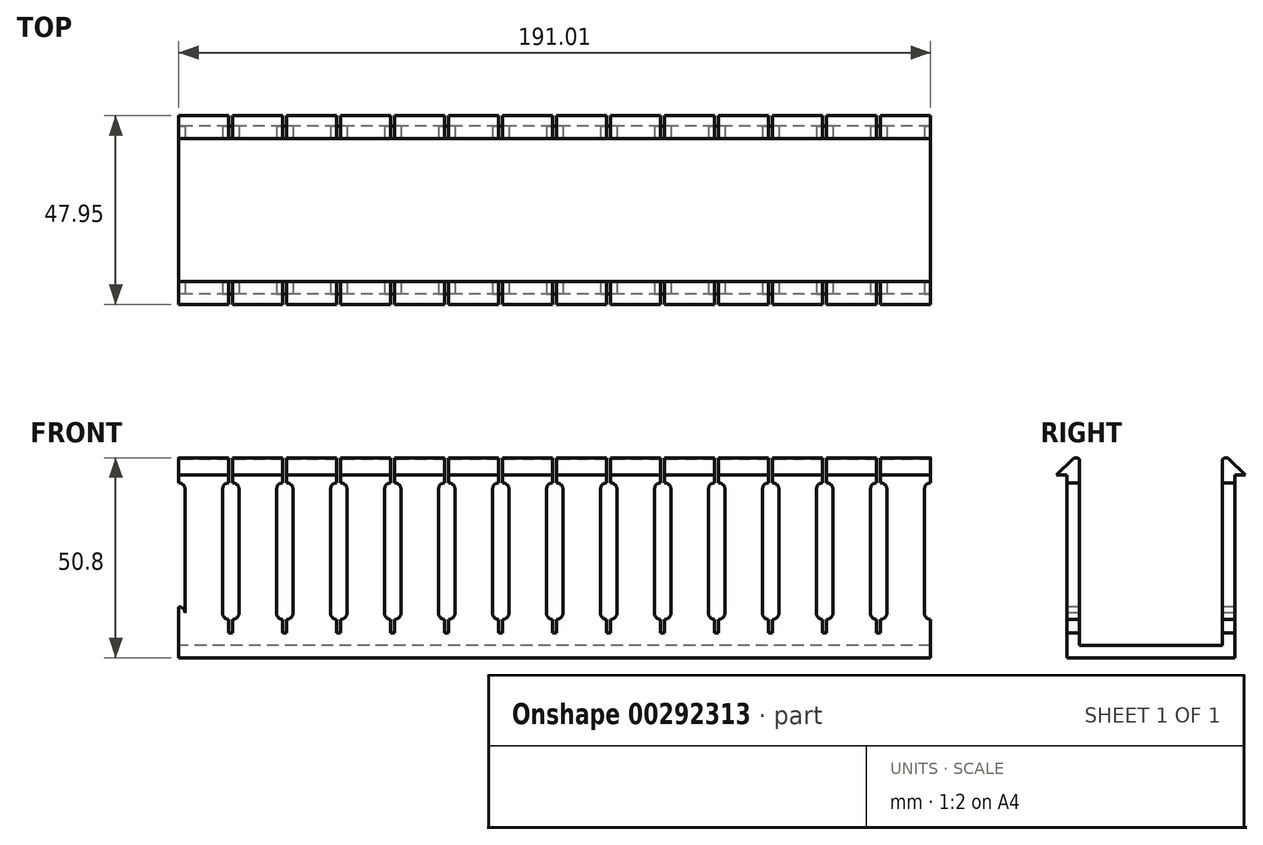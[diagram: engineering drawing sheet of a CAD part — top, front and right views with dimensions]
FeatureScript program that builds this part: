
annotation { "Feature Type Name" : "Feature", "Feature Type Description" : "" }
export const myFeature = defineFeature(function(context is Context, id is Id, definition is map)
    precondition{}
    {
        {
            var Q0;
            Q0=qCreatedBy(makeId("Right.planeOp"),FACE);
            var sketch = newSketch(context, id + "F0", { "sketchPlane" : qUnion([Q0])});
            skLineSegment(sketch, "E0", {"start": v(0, -0.02) * mm, "end": v(0, 46.4) * mm});
            skLineSegment(sketch, "E1", {"start": v(0, 46.4) * mm, "end": v(-2.64, 46.4) * mm});
            skLineSegment(sketch, "E2", {"start": v(-2.64, 46.4) * mm, "end": v(1.38, 50.43) * mm});
            skArc(sketch, "E3", {"start": v(3.17, 50.43) * mm, "mid": v(2.28, 50.8) * mm, "end": v(1.38, 50.43) * mm});
            skLineSegment(sketch, "E4", {"start": v(3.17, 50.43) * mm, "end": v(3.18, 3.18) * mm});
            skLineSegment(sketch, "E5", {"start": v(3.18, 3.18) * mm, "end": v(39.5, 3.18) * mm});
            skLineSegment(sketch, "E6", {"start": v(39.5, 3.18) * mm, "end": v(39.5, 50.43) * mm});
            skArc(sketch, "E7", {"start": v(41.3, 50.43) * mm, "mid": v(40.4, 50.8) * mm, "end": v(39.5, 50.43) * mm});
            skLineSegment(sketch, "E8", {"start": v(41.3, 50.43) * mm, "end": v(45.31, 46.4) * mm});
            skLineSegment(sketch, "E9", {"start": v(45.31, 46.4) * mm, "end": v(42.67, 46.4) * mm});
            skLineSegment(sketch, "E10", {"start": v(42.67, 46.4) * mm, "end": v(42.67, 0) * mm});
            skLineSegment(sketch, "E11", {"start": v(42.67, 0) * mm, "end": v(0, 0) * mm});
            skSolve(sketch);
        }
        {
            var Q0;
            {var subQ0=sQuery(id+"F0.wireOp",EDGE,"E1");Q0=makeQuery(id+"F0.imprint","IMPRINT",FACE,{"disambiguationData":[TD([[makeQuery(id+"F0.imprint","IMPRINT",EDGE,{"derivedFrom":subQ0}),-1.0]])]});}
            extrude(context, id + "F1", {"entities" : qUnion([Q0]), "depth" : 191 * mm});
        }
        {
            var Q0;
            Q0=makeQuery(id+"F1.opExtrude","SWEPT_FACE",FACE,{"disambiguationData":[OSD([sQuery(id+"F0.wireOp",EDGE,"E0")])]});
            var sketch = newSketch(context, id + "F2", { "sketchPlane" : qUnion([Q0])});
            skLineSegment(sketch, "E12", {"start": v(1.59, 42.86) * mm, "end": v(1.59, 11.37) * mm});
            skLineSegment(sketch, "E13", {"start": v(12.7, 50.8) * mm, "end": v(13.72, 50.8) * mm});
            skPoint(sketch, "E14", {"position": v(0, 44.45) * mm});
            skLineSegment(sketch, "E15", {"start": v(0, 44.45) * mm, "end": v(12.7, 44.45) * mm});
            skLineSegment(sketch, "E16", {"start": v(12.7, 50.8) * mm, "end": v(12.7, 44.45) * mm});
            skLineSegment(sketch, "E17", {"start": v(13.72, 50.8) * mm, "end": v(13.72, 44.45) * mm});
            skLineSegment(sketch, "E18", {"start": v(11.11, 42.86) * mm, "end": v(11.11, 11.37) * mm});
            skLineSegment(sketch, "E19", {"start": v(0, 42.86) * mm, "end": v(0, 12.94) * mm});
            skArc(sketch, "E20", {"start": v(1.59, 11.37) * mm, "mid": v(1.12, 12.48) * mm, "end": v(0, 12.94) * mm});
            skArc(sketch, "E21", {"start": v(12.7, 44.45) * mm, "mid": v(11.58, 43.99) * mm, "end": v(11.11, 42.86) * mm});
            skArc(sketch, "E22", {"start": v(15.3, 42.86) * mm, "mid": v(14.84, 43.99) * mm, "end": v(13.72, 44.45) * mm});
            skLineSegment(sketch, "E23", {"start": v(15.3, 42.86) * mm, "end": v(15.3, 11.37) * mm});
            skArc(sketch, "E24", {"start": v(13.72, 9.78) * mm, "mid": v(14.84, 10.24) * mm, "end": v(15.3, 11.37) * mm});
            skLineSegment(sketch, "E25", {"start": v(12.67, 6.3) * mm, "end": v(13.72, 6.3) * mm});
            skLineSegment(sketch, "E26", {"start": v(13.72, 6.3) * mm, "end": v(13.72, 9.78) * mm});
            skLineSegment(sketch, "E27", {"start": v(12.67, 6.3) * mm, "end": v(12.67, 9.78) * mm});
            skArc(sketch, "E28.trimOffspring", {"start": v(11.11, 11.37) * mm, "mid": v(11.57, 10.26) * mm, "end": v(12.67, 9.78) * mm});
            skArc(sketch, "E29.1.0.0", {"start": v(24.83, 11.37) * mm, "mid": v(25.28, 10.26) * mm, "end": v(26.38, 9.78) * mm});
            skLineSegment(sketch, "E29.1.0.1", {"start": v(29.02, 42.86) * mm, "end": v(29.02, 11.37) * mm});
            skArc(sketch, "E29.1.0.2", {"start": v(26.42, 44.45) * mm, "mid": v(25.3, 43.99) * mm, "end": v(24.83, 42.86) * mm});
            skArc(sketch, "E29.1.0.3", {"start": v(29.02, 42.86) * mm, "mid": v(28.55, 43.99) * mm, "end": v(27.43, 44.45) * mm});
            skLineSegment(sketch, "E29.1.0.4", {"start": v(27.43, 50.8) * mm, "end": v(27.43, 44.45) * mm});
            skLineSegment(sketch, "E29.1.0.5", {"start": v(24.83, 42.86) * mm, "end": v(24.83, 11.37) * mm});
            skLineSegment(sketch, "E29.1.0.6", {"start": v(26.38, 6.3) * mm, "end": v(26.38, 9.78) * mm});
            skLineSegment(sketch, "E29.1.0.7", {"start": v(26.42, 50.8) * mm, "end": v(26.42, 44.45) * mm});
            skLineSegment(sketch, "E29.1.0.8", {"start": v(27.43, 6.3) * mm, "end": v(27.43, 9.78) * mm});
            skLineSegment(sketch, "E29.1.0.9", {"start": v(26.42, 50.8) * mm, "end": v(27.43, 50.8) * mm});
            skLineSegment(sketch, "E29.1.0.10", {"start": v(26.38, 6.3) * mm, "end": v(27.43, 6.3) * mm});
            skArc(sketch, "E29.1.0.11", {"start": v(27.43, 9.78) * mm, "mid": v(28.55, 10.24) * mm, "end": v(29.02, 11.37) * mm});
            skArc(sketch, "E29.2.0.0", {"start": v(38.54, 11.37) * mm, "mid": v(39, 10.26) * mm, "end": v(40.1, 9.78) * mm});
            skLineSegment(sketch, "E29.2.0.1", {"start": v(42.74, 42.86) * mm, "end": v(42.74, 11.37) * mm});
            skArc(sketch, "E29.2.0.2", {"start": v(40.13, 44.45) * mm, "mid": v(39, 43.99) * mm, "end": v(38.54, 42.86) * mm});
            skArc(sketch, "E29.2.0.3", {"start": v(42.74, 42.86) * mm, "mid": v(42.27, 43.99) * mm, "end": v(41.15, 44.45) * mm});
            skLineSegment(sketch, "E29.2.0.4", {"start": v(41.15, 50.8) * mm, "end": v(41.15, 44.45) * mm});
            skLineSegment(sketch, "E29.2.0.5", {"start": v(38.54, 42.86) * mm, "end": v(38.54, 11.37) * mm});
            skLineSegment(sketch, "E29.2.0.6", {"start": v(40.1, 6.3) * mm, "end": v(40.1, 9.78) * mm});
            skLineSegment(sketch, "E29.2.0.7", {"start": v(40.13, 50.8) * mm, "end": v(40.13, 44.45) * mm});
            skLineSegment(sketch, "E29.2.0.8", {"start": v(41.15, 6.3) * mm, "end": v(41.15, 9.78) * mm});
            skLineSegment(sketch, "E29.2.0.9", {"start": v(40.13, 50.8) * mm, "end": v(41.15, 50.8) * mm});
            skLineSegment(sketch, "E29.2.0.10", {"start": v(40.1, 6.3) * mm, "end": v(41.15, 6.3) * mm});
            skArc(sketch, "E29.2.0.11", {"start": v(41.15, 9.78) * mm, "mid": v(42.27, 10.24) * mm, "end": v(42.74, 11.37) * mm});
            skArc(sketch, "E29.3.0.0", {"start": v(52.26, 11.37) * mm, "mid": v(52.71, 10.26) * mm, "end": v(53.82, 9.78) * mm});
            skLineSegment(sketch, "E29.3.0.1", {"start": v(56.45, 42.86) * mm, "end": v(56.45, 11.37) * mm});
            skArc(sketch, "E29.3.0.2", {"start": v(53.85, 44.45) * mm, "mid": v(52.73, 43.99) * mm, "end": v(52.26, 42.86) * mm});
            skArc(sketch, "E29.3.0.3", {"start": v(56.45, 42.86) * mm, "mid": v(55.99, 43.99) * mm, "end": v(54.86, 44.45) * mm});
            skLineSegment(sketch, "E29.3.0.4", {"start": v(54.86, 50.8) * mm, "end": v(54.86, 44.45) * mm});
            skLineSegment(sketch, "E29.3.0.5", {"start": v(52.26, 42.86) * mm, "end": v(52.26, 11.37) * mm});
            skLineSegment(sketch, "E29.3.0.6", {"start": v(53.82, 6.3) * mm, "end": v(53.82, 9.78) * mm});
            skLineSegment(sketch, "E29.3.0.7", {"start": v(53.85, 50.8) * mm, "end": v(53.85, 44.45) * mm});
            skLineSegment(sketch, "E29.3.0.8", {"start": v(54.86, 6.3) * mm, "end": v(54.86, 9.78) * mm});
            skLineSegment(sketch, "E29.3.0.9", {"start": v(53.85, 50.8) * mm, "end": v(54.86, 50.8) * mm});
            skLineSegment(sketch, "E29.3.0.10", {"start": v(53.82, 6.3) * mm, "end": v(54.86, 6.3) * mm});
            skArc(sketch, "E29.3.0.11", {"start": v(54.86, 9.78) * mm, "mid": v(55.99, 10.24) * mm, "end": v(56.45, 11.37) * mm});
            skArc(sketch, "E29.4.0.0", {"start": v(65.98, 11.37) * mm, "mid": v(66.43, 10.26) * mm, "end": v(67.53, 9.78) * mm});
            skLineSegment(sketch, "E29.4.0.1", {"start": v(70.17, 42.86) * mm, "end": v(70.17, 11.37) * mm});
            skArc(sketch, "E29.4.0.2", {"start": v(67.56, 44.45) * mm, "mid": v(66.44, 43.99) * mm, "end": v(65.98, 42.86) * mm});
            skArc(sketch, "E29.4.0.3", {"start": v(70.17, 42.86) * mm, "mid": v(69.7, 43.99) * mm, "end": v(68.58, 44.45) * mm});
            skLineSegment(sketch, "E29.4.0.4", {"start": v(68.58, 50.8) * mm, "end": v(68.58, 44.45) * mm});
            skLineSegment(sketch, "E29.4.0.5", {"start": v(65.98, 42.86) * mm, "end": v(65.98, 11.37) * mm});
            skLineSegment(sketch, "E29.4.0.6", {"start": v(67.53, 6.3) * mm, "end": v(67.53, 9.78) * mm});
            skLineSegment(sketch, "E29.4.0.7", {"start": v(67.56, 50.8) * mm, "end": v(67.56, 44.45) * mm});
            skLineSegment(sketch, "E29.4.0.8", {"start": v(68.58, 6.3) * mm, "end": v(68.58, 9.78) * mm});
            skLineSegment(sketch, "E29.4.0.9", {"start": v(67.56, 50.8) * mm, "end": v(68.58, 50.8) * mm});
            skLineSegment(sketch, "E29.4.0.10", {"start": v(67.53, 6.3) * mm, "end": v(68.58, 6.3) * mm});
            skArc(sketch, "E29.4.0.11", {"start": v(68.58, 9.78) * mm, "mid": v(69.7, 10.24) * mm, "end": v(70.17, 11.37) * mm});
            skArc(sketch, "E29.5.0.0", {"start": v(79.7, 11.37) * mm, "mid": v(80.15, 10.26) * mm, "end": v(81.25, 9.78) * mm});
            skLineSegment(sketch, "E29.5.0.1", {"start": v(83.88, 42.86) * mm, "end": v(83.88, 11.37) * mm});
            skArc(sketch, "E29.5.0.2", {"start": v(81.28, 44.45) * mm, "mid": v(80.16, 43.99) * mm, "end": v(79.7, 42.86) * mm});
            skArc(sketch, "E29.5.0.3", {"start": v(83.88, 42.86) * mm, "mid": v(83.42, 43.99) * mm, "end": v(82.3, 44.45) * mm});
            skLineSegment(sketch, "E29.5.0.4", {"start": v(82.3, 50.8) * mm, "end": v(82.3, 44.45) * mm});
            skLineSegment(sketch, "E29.5.0.5", {"start": v(79.7, 42.86) * mm, "end": v(79.7, 11.37) * mm});
            skLineSegment(sketch, "E29.5.0.6", {"start": v(81.25, 6.3) * mm, "end": v(81.25, 9.78) * mm});
            skLineSegment(sketch, "E29.5.0.7", {"start": v(81.28, 50.8) * mm, "end": v(81.28, 44.45) * mm});
            skLineSegment(sketch, "E29.5.0.8", {"start": v(82.3, 6.3) * mm, "end": v(82.3, 9.78) * mm});
            skLineSegment(sketch, "E29.5.0.9", {"start": v(81.28, 50.8) * mm, "end": v(82.3, 50.8) * mm});
            skLineSegment(sketch, "E29.5.0.10", {"start": v(81.25, 6.3) * mm, "end": v(82.3, 6.3) * mm});
            skArc(sketch, "E29.5.0.11", {"start": v(82.3, 9.78) * mm, "mid": v(83.42, 10.24) * mm, "end": v(83.88, 11.37) * mm});
            skArc(sketch, "E29.6.0.0", {"start": v(93.4, 11.37) * mm, "mid": v(93.86, 10.26) * mm, "end": v(94.96, 9.78) * mm});
            skLineSegment(sketch, "E29.6.0.1", {"start": v(97.6, 42.86) * mm, "end": v(97.6, 11.37) * mm});
            skArc(sketch, "E29.6.0.2", {"start": v(95, 44.45) * mm, "mid": v(93.87, 43.99) * mm, "end": v(93.4, 42.86) * mm});
            skArc(sketch, "E29.6.0.3", {"start": v(97.6, 42.86) * mm, "mid": v(97.13, 43.99) * mm, "end": v(96.01, 44.45) * mm});
            skLineSegment(sketch, "E29.6.0.4", {"start": v(96.01, 50.8) * mm, "end": v(96.01, 44.45) * mm});
            skLineSegment(sketch, "E29.6.0.5", {"start": v(93.4, 42.86) * mm, "end": v(93.4, 11.37) * mm});
            skLineSegment(sketch, "E29.6.0.6", {"start": v(94.96, 6.3) * mm, "end": v(94.96, 9.78) * mm});
            skLineSegment(sketch, "E29.6.0.7", {"start": v(95, 50.8) * mm, "end": v(95, 44.45) * mm});
            skLineSegment(sketch, "E29.6.0.8", {"start": v(96.01, 6.3) * mm, "end": v(96.01, 9.78) * mm});
            skLineSegment(sketch, "E29.6.0.9", {"start": v(95, 50.8) * mm, "end": v(96.01, 50.8) * mm});
            skLineSegment(sketch, "E29.6.0.10", {"start": v(94.96, 6.3) * mm, "end": v(96.01, 6.3) * mm});
            skArc(sketch, "E29.6.0.11", {"start": v(96.01, 9.78) * mm, "mid": v(97.13, 10.24) * mm, "end": v(97.6, 11.37) * mm});
            skArc(sketch, "E29.7.0.0", {"start": v(107.12, 11.37) * mm, "mid": v(107.58, 10.26) * mm, "end": v(108.68, 9.78) * mm});
            skLineSegment(sketch, "E29.7.0.1", {"start": v(111.32, 42.86) * mm, "end": v(111.32, 11.37) * mm});
            skArc(sketch, "E29.7.0.2", {"start": v(108.71, 44.45) * mm, "mid": v(107.59, 43.99) * mm, "end": v(107.12, 42.86) * mm});
            skArc(sketch, "E29.7.0.3", {"start": v(111.32, 42.86) * mm, "mid": v(110.85, 43.99) * mm, "end": v(109.73, 44.45) * mm});
            skLineSegment(sketch, "E29.7.0.4", {"start": v(109.73, 50.8) * mm, "end": v(109.73, 44.45) * mm});
            skLineSegment(sketch, "E29.7.0.5", {"start": v(107.12, 42.86) * mm, "end": v(107.12, 11.37) * mm});
            skLineSegment(sketch, "E29.7.0.6", {"start": v(108.68, 6.3) * mm, "end": v(108.68, 9.78) * mm});
            skLineSegment(sketch, "E29.7.0.7", {"start": v(108.71, 50.8) * mm, "end": v(108.71, 44.45) * mm});
            skLineSegment(sketch, "E29.7.0.8", {"start": v(109.73, 6.3) * mm, "end": v(109.73, 9.78) * mm});
            skLineSegment(sketch, "E29.7.0.9", {"start": v(108.71, 50.8) * mm, "end": v(109.73, 50.8) * mm});
            skLineSegment(sketch, "E29.7.0.10", {"start": v(108.68, 6.3) * mm, "end": v(109.73, 6.3) * mm});
            skArc(sketch, "E29.7.0.11", {"start": v(109.73, 9.78) * mm, "mid": v(110.85, 10.24) * mm, "end": v(111.32, 11.37) * mm});
            skArc(sketch, "E29.8.0.0", {"start": v(120.84, 11.37) * mm, "mid": v(121.3, 10.26) * mm, "end": v(122.4, 9.78) * mm});
            skLineSegment(sketch, "E29.8.0.1", {"start": v(125.03, 42.86) * mm, "end": v(125.03, 11.37) * mm});
            skArc(sketch, "E29.8.0.2", {"start": v(122.43, 44.45) * mm, "mid": v(121.3, 43.99) * mm, "end": v(120.84, 42.86) * mm});
            skArc(sketch, "E29.8.0.3", {"start": v(125.03, 42.86) * mm, "mid": v(124.57, 43.99) * mm, "end": v(123.44, 44.45) * mm});
            skLineSegment(sketch, "E29.8.0.4", {"start": v(123.44, 50.8) * mm, "end": v(123.44, 44.45) * mm});
            skLineSegment(sketch, "E29.8.0.5", {"start": v(120.84, 42.86) * mm, "end": v(120.84, 11.37) * mm});
            skLineSegment(sketch, "E29.8.0.6", {"start": v(122.4, 6.3) * mm, "end": v(122.4, 9.78) * mm});
            skLineSegment(sketch, "E29.8.0.7", {"start": v(122.43, 50.8) * mm, "end": v(122.43, 44.45) * mm});
            skLineSegment(sketch, "E29.8.0.8", {"start": v(123.44, 6.3) * mm, "end": v(123.44, 9.78) * mm});
            skLineSegment(sketch, "E29.8.0.9", {"start": v(122.43, 50.8) * mm, "end": v(123.44, 50.8) * mm});
            skLineSegment(sketch, "E29.8.0.10", {"start": v(122.4, 6.3) * mm, "end": v(123.44, 6.3) * mm});
            skArc(sketch, "E29.8.0.11", {"start": v(123.44, 9.78) * mm, "mid": v(124.57, 10.24) * mm, "end": v(125.03, 11.37) * mm});
            skArc(sketch, "E29.9.0.0", {"start": v(134.56, 11.37) * mm, "mid": v(135.01, 10.26) * mm, "end": v(136.11, 9.78) * mm});
            skLineSegment(sketch, "E29.9.0.1", {"start": v(138.75, 42.86) * mm, "end": v(138.75, 11.37) * mm});
            skArc(sketch, "E29.9.0.2", {"start": v(136.14, 44.45) * mm, "mid": v(135.02, 43.99) * mm, "end": v(134.56, 42.86) * mm});
            skArc(sketch, "E29.9.0.3", {"start": v(138.75, 42.86) * mm, "mid": v(138.28, 43.99) * mm, "end": v(137.16, 44.45) * mm});
            skLineSegment(sketch, "E29.9.0.4", {"start": v(137.16, 50.8) * mm, "end": v(137.16, 44.45) * mm});
            skLineSegment(sketch, "E29.9.0.5", {"start": v(134.56, 42.86) * mm, "end": v(134.56, 11.37) * mm});
            skLineSegment(sketch, "E29.9.0.6", {"start": v(136.11, 6.3) * mm, "end": v(136.11, 9.78) * mm});
            skLineSegment(sketch, "E29.9.0.7", {"start": v(136.14, 50.8) * mm, "end": v(136.14, 44.45) * mm});
            skLineSegment(sketch, "E29.9.0.8", {"start": v(137.16, 6.3) * mm, "end": v(137.16, 9.78) * mm});
            skLineSegment(sketch, "E29.9.0.9", {"start": v(136.14, 50.8) * mm, "end": v(137.16, 50.8) * mm});
            skLineSegment(sketch, "E29.9.0.10", {"start": v(136.11, 6.3) * mm, "end": v(137.16, 6.3) * mm});
            skArc(sketch, "E29.9.0.11", {"start": v(137.16, 9.78) * mm, "mid": v(138.28, 10.24) * mm, "end": v(138.75, 11.37) * mm});
            skLineSegment(sketch, "E29.direction1", {"start": v(12.67, 6.3) * mm, "end": v(26.38, 6.3) * mm, "construction": true});
            skArc(sketch, "E30.0.10.0", {"start": v(148.27, 11.37) * mm, "mid": v(148.73, 10.26) * mm, "end": v(149.83, 9.78) * mm});
            skLineSegment(sketch, "E30.4.10.0", {"start": v(152.46, 42.86) * mm, "end": v(152.46, 11.37) * mm});
            skArc(sketch, "E30.7.10.0", {"start": v(149.86, 44.45) * mm, "mid": v(148.74, 43.99) * mm, "end": v(148.27, 42.86) * mm});
            skArc(sketch, "E30.11.10.0", {"start": v(152.46, 42.86) * mm, "mid": v(152, 43.99) * mm, "end": v(150.88, 44.45) * mm});
            skLineSegment(sketch, "E30.15.10.0", {"start": v(150.88, 50.8) * mm, "end": v(150.88, 44.45) * mm});
            skLineSegment(sketch, "E30.18.10.0", {"start": v(148.27, 42.86) * mm, "end": v(148.27, 11.37) * mm});
            skLineSegment(sketch, "E30.21.10.0", {"start": v(149.83, 6.3) * mm, "end": v(149.83, 9.78) * mm});
            skLineSegment(sketch, "E30.24.10.0", {"start": v(149.86, 50.8) * mm, "end": v(149.86, 44.45) * mm});
            skLineSegment(sketch, "E30.27.10.0", {"start": v(150.88, 6.3) * mm, "end": v(150.88, 9.78) * mm});
            skLineSegment(sketch, "E30.30.10.0", {"start": v(149.86, 50.8) * mm, "end": v(150.88, 50.8) * mm});
            skLineSegment(sketch, "E30.33.10.0", {"start": v(149.83, 6.3) * mm, "end": v(150.88, 6.3) * mm});
            skArc(sketch, "E30.36.10.0", {"start": v(150.88, 9.78) * mm, "mid": v(152, 10.24) * mm, "end": v(152.46, 11.37) * mm});
            skArc(sketch, "E30.0.11.0", {"start": v(161.99, 11.37) * mm, "mid": v(162.44, 10.26) * mm, "end": v(163.54, 9.78) * mm});
            skLineSegment(sketch, "E30.4.11.0", {"start": v(166.18, 42.86) * mm, "end": v(166.18, 11.37) * mm});
            skArc(sketch, "E30.7.11.0", {"start": v(163.58, 44.45) * mm, "mid": v(162.45, 43.99) * mm, "end": v(161.99, 42.86) * mm});
            skArc(sketch, "E30.11.11.0", {"start": v(166.18, 42.86) * mm, "mid": v(165.71, 43.99) * mm, "end": v(164.6, 44.45) * mm});
            skLineSegment(sketch, "E30.15.11.0", {"start": v(164.6, 50.8) * mm, "end": v(164.6, 44.45) * mm});
            skLineSegment(sketch, "E30.18.11.0", {"start": v(161.99, 42.86) * mm, "end": v(161.99, 11.37) * mm});
            skLineSegment(sketch, "E30.21.11.0", {"start": v(163.54, 6.3) * mm, "end": v(163.54, 9.78) * mm});
            skLineSegment(sketch, "E30.24.11.0", {"start": v(163.58, 50.8) * mm, "end": v(163.58, 44.45) * mm});
            skLineSegment(sketch, "E30.27.11.0", {"start": v(164.6, 6.3) * mm, "end": v(164.6, 9.78) * mm});
            skLineSegment(sketch, "E30.30.11.0", {"start": v(163.58, 50.8) * mm, "end": v(164.6, 50.8) * mm});
            skLineSegment(sketch, "E30.33.11.0", {"start": v(163.54, 6.3) * mm, "end": v(164.6, 6.3) * mm});
            skArc(sketch, "E30.36.11.0", {"start": v(164.6, 9.78) * mm, "mid": v(165.71, 10.24) * mm, "end": v(166.18, 11.37) * mm});
            skArc(sketch, "E30.0.12.0", {"start": v(175.7, 11.37) * mm, "mid": v(176.16, 10.26) * mm, "end": v(177.26, 9.78) * mm});
            skLineSegment(sketch, "E30.4.12.0", {"start": v(179.9, 42.86) * mm, "end": v(179.9, 11.37) * mm});
            skArc(sketch, "E30.7.12.0", {"start": v(177.3, 44.45) * mm, "mid": v(176.17, 43.99) * mm, "end": v(175.7, 42.86) * mm});
            skArc(sketch, "E30.11.12.0", {"start": v(179.9, 42.86) * mm, "mid": v(179.43, 43.99) * mm, "end": v(178.3, 44.45) * mm});
            skLineSegment(sketch, "E30.15.12.0", {"start": v(178.3, 50.8) * mm, "end": v(178.3, 44.45) * mm});
            skLineSegment(sketch, "E30.18.12.0", {"start": v(175.7, 42.86) * mm, "end": v(175.7, 11.37) * mm});
            skLineSegment(sketch, "E30.21.12.0", {"start": v(177.26, 6.3) * mm, "end": v(177.26, 9.78) * mm});
            skLineSegment(sketch, "E30.24.12.0", {"start": v(177.3, 50.8) * mm, "end": v(177.3, 44.45) * mm});
            skLineSegment(sketch, "E30.27.12.0", {"start": v(178.3, 6.3) * mm, "end": v(178.3, 9.78) * mm});
            skLineSegment(sketch, "E30.30.12.0", {"start": v(177.3, 50.8) * mm, "end": v(178.3, 50.8) * mm});
            skLineSegment(sketch, "E30.33.12.0", {"start": v(177.26, 6.3) * mm, "end": v(178.3, 6.3) * mm});
            skArc(sketch, "E30.36.12.0", {"start": v(178.3, 9.78) * mm, "mid": v(179.43, 10.24) * mm, "end": v(179.9, 11.37) * mm});
            skArc(sketch, "E30.0.13.0", {"start": v(189.42, 11.37) * mm, "mid": v(189.87, 10.26) * mm, "end": v(190.98, 9.78) * mm});
            skLineSegment(sketch, "E30.4.13.0", {"start": v(193.61, 42.86) * mm, "end": v(193.61, 11.37) * mm});
            skArc(sketch, "E30.7.13.0", {"start": v(191, 44.45) * mm, "mid": v(189.89, 43.99) * mm, "end": v(189.42, 42.86) * mm});
            skArc(sketch, "E30.11.13.0", {"start": v(193.61, 42.86) * mm, "mid": v(193.15, 43.99) * mm, "end": v(192.02, 44.45) * mm});
            skLineSegment(sketch, "E30.15.13.0", {"start": v(192.02, 50.8) * mm, "end": v(192.02, 44.45) * mm});
            skLineSegment(sketch, "E30.18.13.0", {"start": v(189.42, 42.86) * mm, "end": v(189.42, 11.37) * mm});
            skLineSegment(sketch, "E30.21.13.0", {"start": v(190.98, 6.3) * mm, "end": v(190.98, 9.78) * mm});
            skLineSegment(sketch, "E30.24.13.0", {"start": v(191, 50.8) * mm, "end": v(191, 44.45) * mm});
            skLineSegment(sketch, "E30.27.13.0", {"start": v(192.02, 6.3) * mm, "end": v(192.02, 9.78) * mm});
            skLineSegment(sketch, "E30.30.13.0", {"start": v(191, 50.8) * mm, "end": v(192.02, 50.8) * mm});
            skLineSegment(sketch, "E30.33.13.0", {"start": v(190.98, 6.3) * mm, "end": v(192.02, 6.3) * mm});
            skArc(sketch, "E30.36.13.0", {"start": v(192.02, 9.78) * mm, "mid": v(193.15, 10.24) * mm, "end": v(193.61, 11.37) * mm});
            skArc(sketch, "E31", {"start": v(1.59, 42.86) * mm, "mid": v(1.12, 43.99) * mm, "end": v(0, 44.45) * mm});
            skSolve(sketch);
        }
        {
            var Q0;
            {var subQ0=sQuery(id+"F2.wireOp",EDGE,"E13");Q0=makeQuery(id+"F2.imprint","IMPRINT",FACE,{"disambiguationData":[TD([[makeQuery(id+"F2.imprint","IMPRINT",EDGE,{"derivedFrom":subQ0}),-1.0]])]});}
            var Q1;
            Q1=makeQuery(id+"F2.imprint","IMPRINT",FACE,{"disambiguationData":[TD([[makeQuery(id+"F2.imprint","IMPRINT",EDGE,{"derivedFrom":sQuery(id+"F2.wireOp",EDGE,"E18")}),1.0]])]});
            var Q2;
            {var subQ0=sQuery(id+"F2.wireOp",EDGE,"E29.1.0.9");Q2=makeQuery(id+"F2.imprint","IMPRINT",FACE,{"disambiguationData":[TD([[makeQuery(id+"F2.imprint","IMPRINT",EDGE,{"derivedFrom":subQ0}),-1.0]])]});}
            var Q3;
            Q3=makeQuery(id+"F2.imprint","IMPRINT",FACE,{"disambiguationData":[TD([[makeQuery(id+"F2.imprint","IMPRINT",EDGE,{"derivedFrom":sQuery(id+"F2.wireOp",EDGE,"E29.1.0.0")}),1.0]])]});
            var Q4;
            Q4=makeQuery(id+"F2.imprint","IMPRINT",FACE,{"disambiguationData":[TD([[makeQuery(id+"F2.imprint","IMPRINT",EDGE,{"derivedFrom":sQuery(id+"F2.wireOp",EDGE,"E12")}),-1.0]])]});
            var Q5;
            Q5=makeQuery(id+"F2.imprint","IMPRINT",FACE,{"disambiguationData":[TD([[makeQuery(id+"F2.imprint","IMPRINT",EDGE,{"derivedFrom":sQuery(id+"F2.wireOp",EDGE,"E29.2.0.0")}),1.0]])]});
            var Q6;
            {var subQ0=sQuery(id+"F2.wireOp",EDGE,"E29.2.0.9");Q6=makeQuery(id+"F2.imprint","IMPRINT",FACE,{"disambiguationData":[TD([[makeQuery(id+"F2.imprint","IMPRINT",EDGE,{"derivedFrom":subQ0}),-1.0]])]});}
            var Q7;
            Q7=makeQuery(id+"F2.imprint","IMPRINT",FACE,{"disambiguationData":[TD([[makeQuery(id+"F2.imprint","IMPRINT",EDGE,{"derivedFrom":sQuery(id+"F2.wireOp",EDGE,"E29.3.0.0")}),1.0]])]});
            var Q8;
            {var subQ0=sQuery(id+"F2.wireOp",EDGE,"E29.3.0.9");Q8=makeQuery(id+"F2.imprint","IMPRINT",FACE,{"disambiguationData":[TD([[makeQuery(id+"F2.imprint","IMPRINT",EDGE,{"derivedFrom":subQ0}),-1.0]])]});}
            var Q9;
            Q9=makeQuery(id+"F2.imprint","IMPRINT",FACE,{"disambiguationData":[TD([[makeQuery(id+"F2.imprint","IMPRINT",EDGE,{"derivedFrom":sQuery(id+"F2.wireOp",EDGE,"E29.4.0.0")}),1.0]])]});
            var Q10;
            {var subQ0=sQuery(id+"F2.wireOp",EDGE,"E29.4.0.9");Q10=makeQuery(id+"F2.imprint","IMPRINT",FACE,{"disambiguationData":[TD([[makeQuery(id+"F2.imprint","IMPRINT",EDGE,{"derivedFrom":subQ0}),-1.0]])]});}
            var Q11;
            Q11=makeQuery(id+"F2.imprint","IMPRINT",FACE,{"disambiguationData":[TD([[makeQuery(id+"F2.imprint","IMPRINT",EDGE,{"derivedFrom":sQuery(id+"F2.wireOp",EDGE,"E29.5.0.0")}),1.0]])]});
            var Q12;
            {var subQ0=sQuery(id+"F2.wireOp",EDGE,"E29.5.0.9");Q12=makeQuery(id+"F2.imprint","IMPRINT",FACE,{"disambiguationData":[TD([[makeQuery(id+"F2.imprint","IMPRINT",EDGE,{"derivedFrom":subQ0}),-1.0]])]});}
            var Q13;
            Q13=makeQuery(id+"F2.imprint","IMPRINT",FACE,{"disambiguationData":[TD([[makeQuery(id+"F2.imprint","IMPRINT",EDGE,{"derivedFrom":sQuery(id+"F2.wireOp",EDGE,"E29.6.0.0")}),1.0]])]});
            var Q14;
            {var subQ0=sQuery(id+"F2.wireOp",EDGE,"E29.6.0.9");Q14=makeQuery(id+"F2.imprint","IMPRINT",FACE,{"disambiguationData":[TD([[makeQuery(id+"F2.imprint","IMPRINT",EDGE,{"derivedFrom":subQ0}),-1.0]])]});}
            var Q15;
            {var subQ0=sQuery(id+"F2.wireOp",EDGE,"E29.7.0.9");Q15=makeQuery(id+"F2.imprint","IMPRINT",FACE,{"disambiguationData":[TD([[makeQuery(id+"F2.imprint","IMPRINT",EDGE,{"derivedFrom":subQ0}),-1.0]])]});}
            var Q16;
            {var subQ0=sQuery(id+"F2.wireOp",EDGE,"E29.8.0.9");Q16=makeQuery(id+"F2.imprint","IMPRINT",FACE,{"disambiguationData":[TD([[makeQuery(id+"F2.imprint","IMPRINT",EDGE,{"derivedFrom":subQ0}),-1.0]])]});}
            var Q17;
            {var subQ0=sQuery(id+"F2.wireOp",EDGE,"E29.9.0.9");Q17=makeQuery(id+"F2.imprint","IMPRINT",FACE,{"disambiguationData":[TD([[makeQuery(id+"F2.imprint","IMPRINT",EDGE,{"derivedFrom":subQ0}),-1.0]])]});}
            var Q18;
            {var subQ0=sQuery(id+"F2.wireOp",EDGE,"E30.30.10.0");Q18=makeQuery(id+"F2.imprint","IMPRINT",FACE,{"disambiguationData":[TD([[makeQuery(id+"F2.imprint","IMPRINT",EDGE,{"derivedFrom":subQ0}),-1.0]])]});}
            var Q19;
            {var subQ0=sQuery(id+"F2.wireOp",EDGE,"E30.30.11.0");Q19=makeQuery(id+"F2.imprint","IMPRINT",FACE,{"disambiguationData":[TD([[makeQuery(id+"F2.imprint","IMPRINT",EDGE,{"derivedFrom":subQ0}),-1.0]])]});}
            var Q20;
            {var subQ0=sQuery(id+"F2.wireOp",EDGE,"E30.30.12.0");Q20=makeQuery(id+"F2.imprint","IMPRINT",FACE,{"disambiguationData":[TD([[makeQuery(id+"F2.imprint","IMPRINT",EDGE,{"derivedFrom":subQ0}),-1.0]])]});}
            var Q21;
            Q21=makeQuery(id+"F2.imprint","IMPRINT",FACE,{"disambiguationData":[TD([[makeQuery(id+"F2.imprint","IMPRINT",EDGE,{"derivedFrom":sQuery(id+"F2.wireOp",EDGE,"E30.0.13.0")}),1.0]])]});
            var Q22;
            Q22=makeQuery(id+"F2.imprint","IMPRINT",FACE,{"disambiguationData":[TD([[makeQuery(id+"F2.imprint","IMPRINT",EDGE,{"derivedFrom":sQuery(id+"F2.wireOp",EDGE,"E30.0.12.0")}),1.0]])]});
            var Q23;
            Q23=makeQuery(id+"F2.imprint","IMPRINT",FACE,{"disambiguationData":[TD([[makeQuery(id+"F2.imprint","IMPRINT",EDGE,{"derivedFrom":sQuery(id+"F2.wireOp",EDGE,"E30.0.11.0")}),1.0]])]});
            var Q24;
            Q24=makeQuery(id+"F2.imprint","IMPRINT",FACE,{"disambiguationData":[TD([[makeQuery(id+"F2.imprint","IMPRINT",EDGE,{"derivedFrom":sQuery(id+"F2.wireOp",EDGE,"E30.0.10.0")}),1.0]])]});
            var Q25;
            Q25=makeQuery(id+"F2.imprint","IMPRINT",FACE,{"disambiguationData":[TD([[makeQuery(id+"F2.imprint","IMPRINT",EDGE,{"derivedFrom":sQuery(id+"F2.wireOp",EDGE,"E29.9.0.0")}),1.0]])]});
            var Q26;
            Q26=makeQuery(id+"F2.imprint","IMPRINT",FACE,{"disambiguationData":[TD([[makeQuery(id+"F2.imprint","IMPRINT",EDGE,{"derivedFrom":sQuery(id+"F2.wireOp",EDGE,"E29.8.0.0")}),1.0]])]});
            var Q27;
            Q27=makeQuery(id+"F2.imprint","IMPRINT",FACE,{"disambiguationData":[TD([[makeQuery(id+"F2.imprint","IMPRINT",EDGE,{"derivedFrom":sQuery(id+"F2.wireOp",EDGE,"E29.7.0.0")}),1.0]])]});
            extrude(context, id + "F3", {"entities" : qUnion([Q0, Q1, Q2, Q3, Q4, Q5, Q6, Q7, Q8, Q9, Q10, Q11, Q12, Q13, Q14, Q15, Q16, Q17, Q18, Q19, Q20, Q21, Q22, Q23, Q24, Q25, Q26, Q27]), "operationType" : NewBodyOperationType.REMOVE, "endBound" : BoundingType.THROUGH_ALL, "oppositeDirection" : true, "depth" : 25.4 * mm, "hasSecondDirection" : true, "secondDirectionBound" : SecondDirectionBoundingType.THROUGH_ALL, "secondDirectionOppositeDirection" : false, "secondDirectionDepth" : 25.4 * mm});
        }
    });
